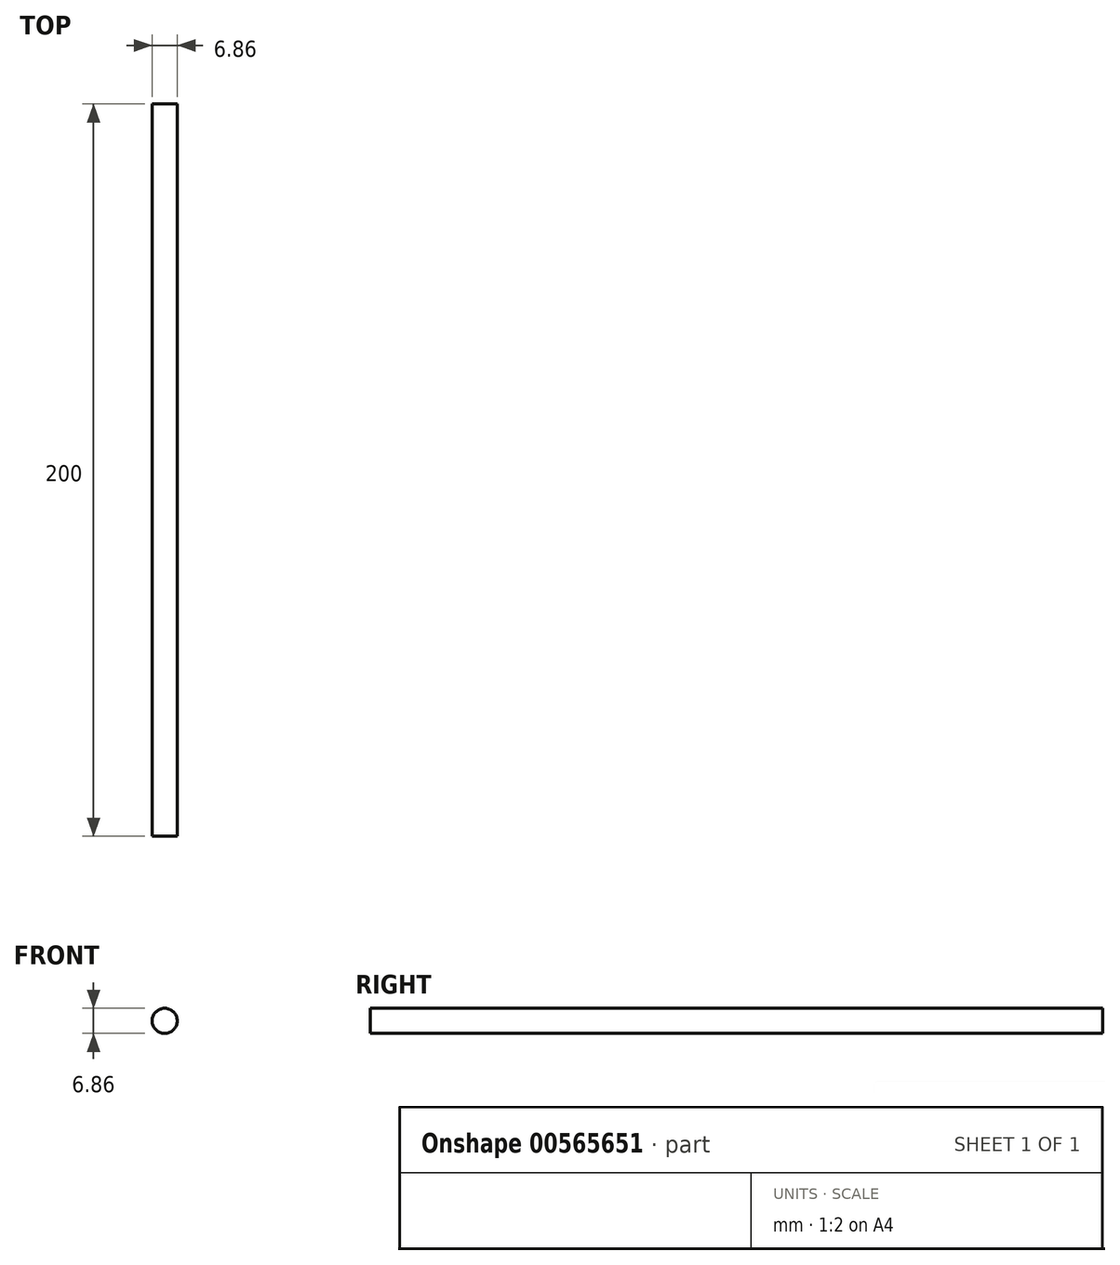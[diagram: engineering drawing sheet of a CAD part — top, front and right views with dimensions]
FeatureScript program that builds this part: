
annotation { "Feature Type Name" : "Feature", "Feature Type Description" : "" }
export const myFeature = defineFeature(function(context is Context, id is Id, definition is map)
    precondition{}
    {
        {
            var Q0;
            Q0=qCreatedBy(makeId("Front.planeOp"),FACE);
            var sketch = newSketch(context, id + "F0", { "sketchPlane" : qUnion([Q0])});
            skCircle(sketch, "E0", {"center": v(0, 0) * mm, "radius": 3.43 * mm});
            skSolve(sketch);
        }
        {
            var Q0;
            Q0=makeQuery(id+"F0.imprint","IMPRINT",FACE,{"disambiguationData":[TD([[makeQuery(id+"F0.imprint","IMPRINT",EDGE,{"derivedFrom":sQuery(id+"F0.wireOp",EDGE,"E0")}),1.0]])]});
            extrude(context, id + "F1", {"entities" : qUnion([Q0]), "depth" : 200 * mm, "offsetDistance" : 25 * mm});
        }
    });
